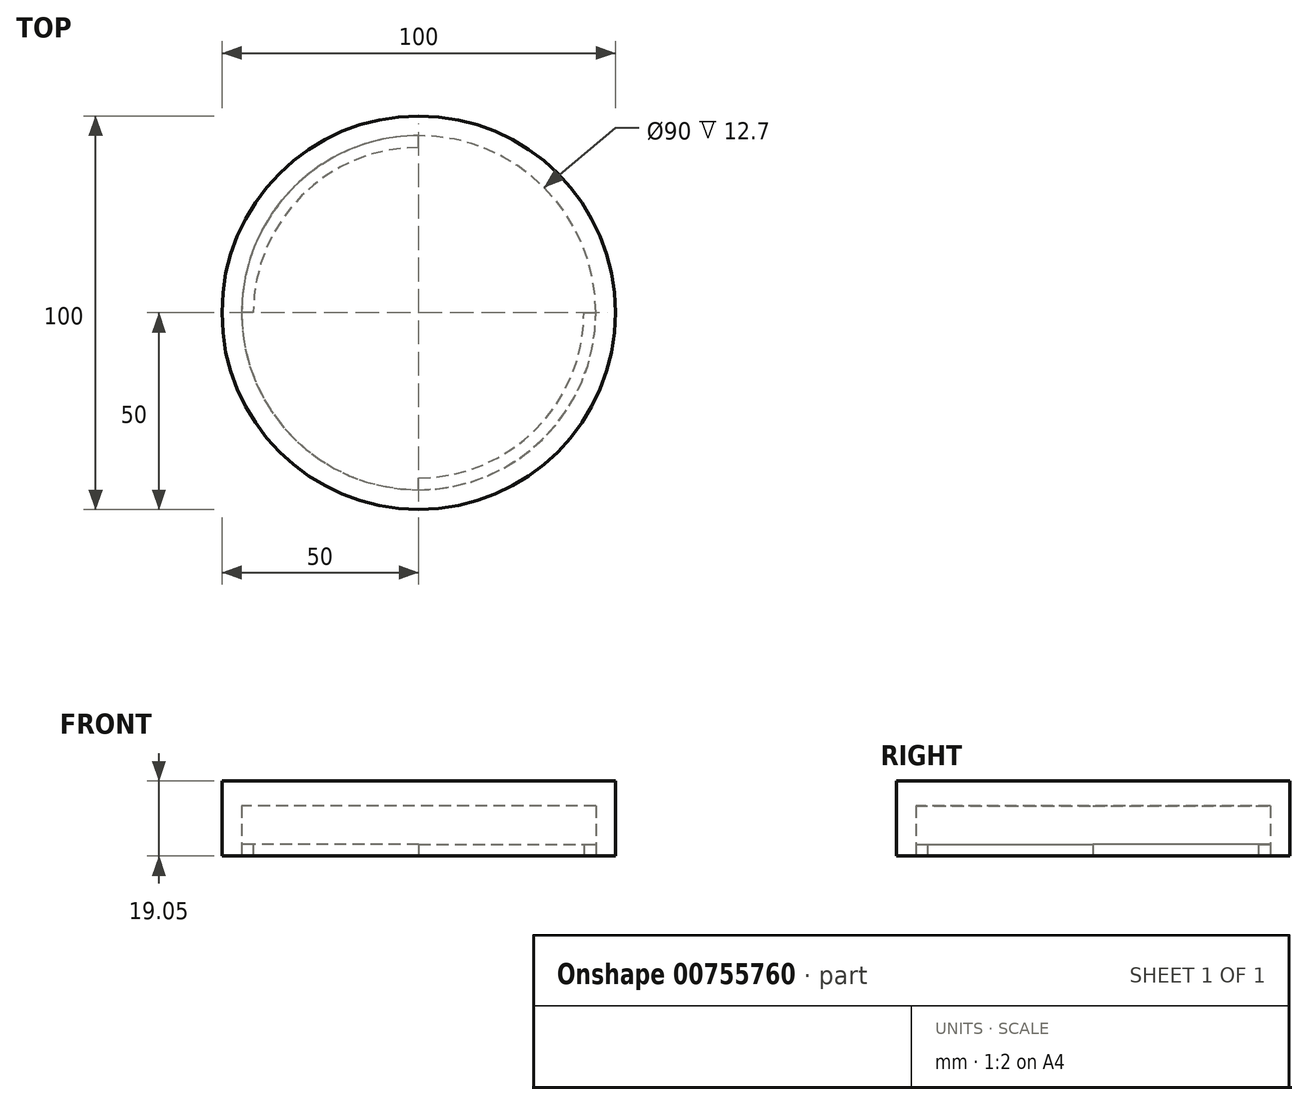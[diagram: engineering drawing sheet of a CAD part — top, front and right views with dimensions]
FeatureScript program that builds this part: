
annotation { "Feature Type Name" : "Feature", "Feature Type Description" : "" }
export const myFeature = defineFeature(function(context is Context, id is Id, definition is map)
    precondition{}
    {
        {
            assignVariable(context, id + "F0", {"name" : "HookWidth", "anyValue" : 3 * mm});
        }
        {
            assignVariable(context, id + "F1", {"name" : "Thickness", "anyValue" : 12.7 * mm});
        }
        {
            var Q0;
            Q0=qCreatedBy(makeId("Top.planeOp"),FACE);
            var sketch = newSketch(context, id + "F2", { "sketchPlane" : qUnion([Q0])});
            skCircle(sketch, "E0", {"center": v(0, 0) * mm, "radius": 50 * mm});
            skCircle(sketch, "E1", {"center": v(0, 0) * mm, "radius": 45 * mm});
            skPoint(sketch, "E2", {"position": v(0, -45) * mm});
            skPoint(sketch, "E3", {"position": v(45, 0) * mm});
            skPoint(sketch, "E4", {"position": v(0, 45) * mm});
            skPoint(sketch, "E5", {"position": v(-45, 0) * mm});
            skPoint(sketch, "E6", {"position": v(0, 42) * mm});
            skCircle(sketch, "E7", {"center": v(0, 0) * mm, "radius": 42 * mm, "construction": true});
            skArc(sketch, "E8", {"start": v(0, -42) * mm, "mid": v(29.7, -29.7) * mm, "end": v(42, 0) * mm});
            skArc(sketch, "E9", {"start": v(0, 42) * mm, "mid": v(-29.7, 29.7) * mm, "end": v(-42, 0) * mm});
            skLineSegment(sketch, "E10", {"start": v(0, 42) * mm, "end": v(0, 45) * mm});
            skLineSegment(sketch, "E11", {"start": v(-42, 0) * mm, "end": v(-45, 0) * mm});
            skLineSegment(sketch, "E12", {"start": v(42, 0) * mm, "end": v(45, 0) * mm});
            skLineSegment(sketch, "E13", {"start": v(0, -45) * mm, "end": v(0, -42) * mm});
            skSolve(sketch);
        }
        {
            var Q0;
            Q0=makeQuery(id+"F2.imprint","IMPRINT",FACE,{"disambiguationData":[TD([[makeQuery(id+"F2.imprint","IMPRINT",EDGE,{"derivedFrom":sQuery(id+"F2.wireOp",EDGE,"E9")}),-1.0]])]});
            var Q1;
            Q1=makeQuery(id+"F2.imprint","IMPRINT",FACE,{"disambiguationData":[TD([[makeQuery(id+"F2.imprint","IMPRINT",EDGE,{"derivedFrom":sQuery(id+"F2.wireOp",EDGE,"E8")}),-1.0]])]});
            extrude(context, id + "F3", {"entities" : qUnion([Q0, Q1]), "depth" : getVariable(context, 'HookWidth'), "offsetDistance" : 25 * mm});
        }
        {
            var Q0;
            Q0=makeQuery(id+"F2.imprint","IMPRINT",FACE,{"disambiguationData":[TD([[makeQuery(id+"F2.imprint","IMPRINT",EDGE,{"derivedFrom":sQuery(id+"F2.wireOp",EDGE,"E0")}),1.0]])]});
            extrude(context, id + "F4", {"entities" : qUnion([Q0]), "operationType" : NewBodyOperationType.ADD, "depth" : getVariable(context, 'Thickness'), "offsetDistance" : 25 * mm});
        }
        {
            var Q0;
            Q0=makeQuery(id+"F4.opExtrude","CAP_FACE",FACE,{"disambiguationData":[OSD([sQuery(id+"F2.wireOp",EDGE,"E0"),sQuery(id+"F2.wireOp",EDGE,"E1")])],"isStart":false});
            var sketch = newSketch(context, id + "F5", { "sketchPlane" : qUnion([Q0])});
            skCircle(sketch, "E14", {"center": v(0, 0) * mm, "radius": 50 * mm});
            skSolve(sketch);
        }
        {
            var Q0;
            Q0=makeQuery(id+"F5.imprint","IMPRINT",FACE,{"disambiguationData":[TD([[makeQuery(id+"F5.imprint","IMPRINT",EDGE,{"derivedFrom":sQuery(id+"F5.wireOp",EDGE,"E14")}),1.0]])]});
            var Q1;
            Q1=makeQuery(id+"F5.imprint","IMPRINT",FACE,{"disambiguationData":[TD([[makeQuery(id+"F5.imprint","IMPRINT",EDGE,{"derivedFrom":makeQuery(id+"F4.opExtrude","CAP_EDGE",EDGE,{"disambiguationData":[OSD([sQuery(id+"F2.wireOp",EDGE,"E1")])],"isStart":false})}),1.0]])]});
            extrude(context, id + "F6", {"entities" : qUnion([Q0, Q1]), "operationType" : NewBodyOperationType.ADD, "depth" : getVariable(context, 'Thickness') / 2, "offsetDistance" : 25 * mm});
        }
    });
